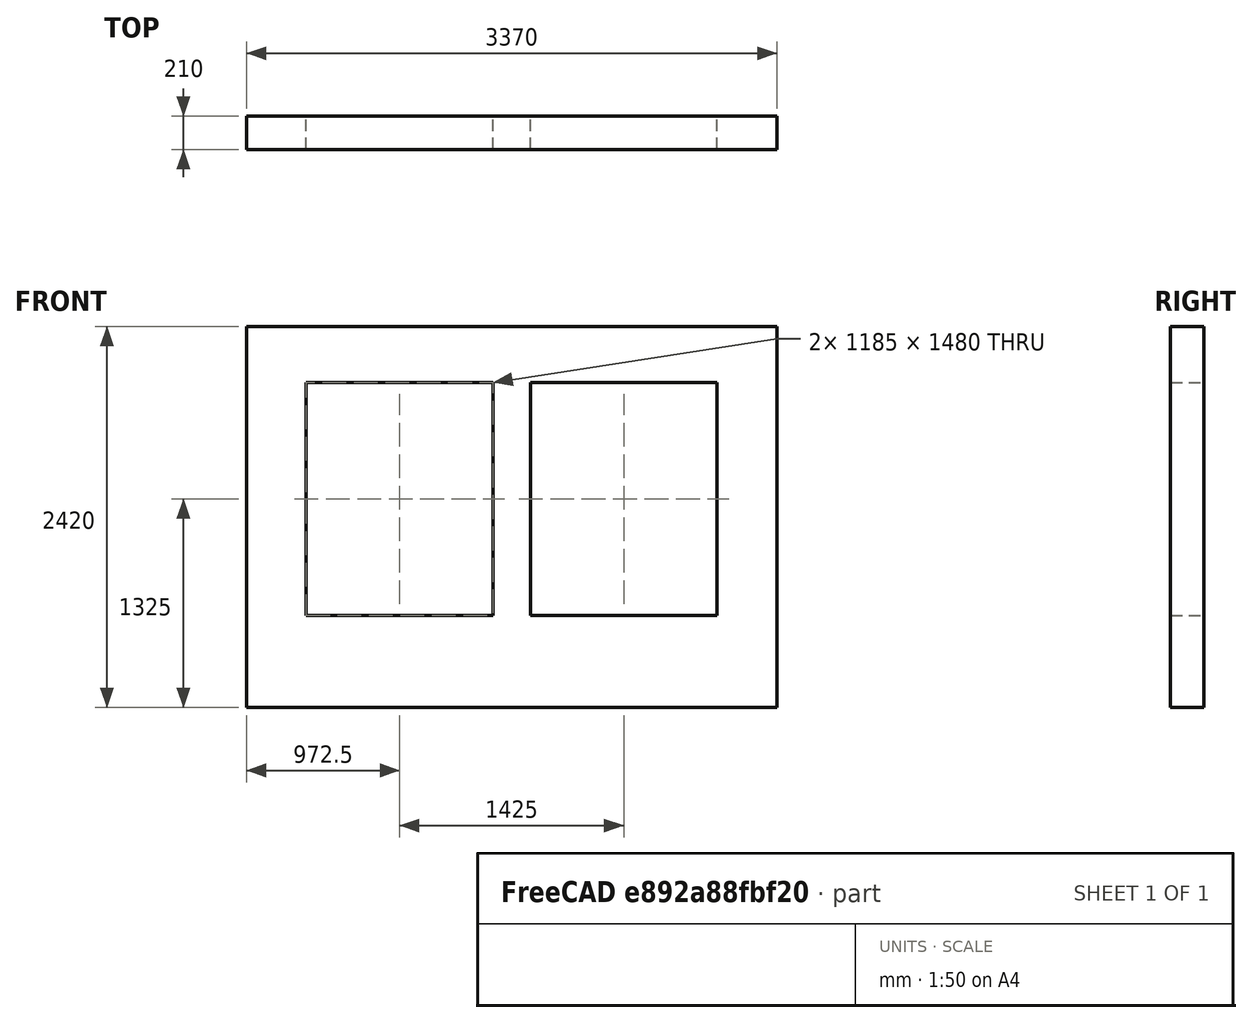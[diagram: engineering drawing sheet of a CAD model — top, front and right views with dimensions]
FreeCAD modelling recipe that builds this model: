
FCSTD DOCUMENT  (FreeCAD 0.19R24276 (Git))
Label: frontWall
License: All rights reserved
LicenseURL: http://en.wikipedia.org/wiki/All_rights_reserved
objects: Sketcher::SketchObject×1, PartDesign::Pad×1, PartDesign::Body×1
note: 4 computed .brp shape members not serialized (recipe doc carries the construction recipe); baked Part::Feature solids carry a one-line shape summary decoded from their .brp

FEATURE [Sketcher::SketchObject] Sketch
  FullyConstrained = true
  MapMode = 5
  Placement = pos=(0,0,0) rot=(1,0,0;1.5708rad)
  Support = -> [XZ_Plane]
  sketch-geometry (12):
    g0: LineSegment StartX=0 StartY=0 StartZ=0 EndX=3370 EndY=0 EndZ=0
    g1: LineSegment StartX=3370 StartY=0 StartZ=0 EndX=3370 EndY=2420 EndZ=0
    g2: LineSegment StartX=3370 StartY=2420 StartZ=0 EndX=0 EndY=2420 EndZ=0
    g3: LineSegment StartX=0 StartY=2420 StartZ=0 EndX=0 EndY=0 EndZ=0
    g4: LineSegment StartX=380 StartY=2065 StartZ=0 EndX=1565 EndY=2065 EndZ=0
    g5: LineSegment StartX=1565 StartY=2065 StartZ=0 EndX=1565 EndY=585 EndZ=0
    g6: LineSegment StartX=1565 StartY=585 StartZ=0 EndX=380 EndY=585 EndZ=0
    g7: LineSegment StartX=380 StartY=585 StartZ=0 EndX=380 EndY=2065 EndZ=0
    g8: LineSegment StartX=1805 StartY=2065 StartZ=0 EndX=2990 EndY=2065 EndZ=0
    g9: LineSegment StartX=2990 StartY=2065 StartZ=0 EndX=2990 EndY=585 EndZ=0
    g10: LineSegment StartX=2990 StartY=585 StartZ=0 EndX=1805 EndY=585 EndZ=0
    g11: LineSegment StartX=1805 StartY=585 StartZ=0 EndX=1805 EndY=2065 EndZ=0
  constraints (35):
    c: Coincident(g0,g1)
    c: Coincident(g1,g2)
    c: Coincident(g2,g3)
    c: Coincident(g3,g0)
    c: Horizontal(g0)
    c: Horizontal(g2)
    c: Vertical(g1)
    c: Vertical(g3)
    c: Coincident(g0,g-1)
    c: DistanceX(g0,g0) = 3370
    c: DistanceY(g3,g3) = 2420
    c: Coincident(g4,g5)
    c: Coincident(g5,g6)
    c: Coincident(g6,g7)
    c: Coincident(g7,g4)
    c: Horizontal(g4)
    c: Horizontal(g6)
    c: Vertical(g5)
    c: Vertical(g7)
    c: Coincident(g8,g9)
    c: Coincident(g9,g10)
    c: Coincident(g10,g11)
    c: Coincident(g11,g8)
    c: Horizontal(g8)
    c: Horizontal(g10)
    c: Vertical(g9)
    c: Vertical(g11)
    c: DistanceY(g0,g6) = 585
    c: Horizontal(g10,g5)
    c: DistanceX(g0,g6) = 380
    c: DistanceY(g6,g4) = 1480
    c: Equal(g7,g11)
    c: DistanceX(g6,g5) = 1185
    c: Equal(g6,g10)
    c: DistanceX(g5,g10) = 240
FEATURE [PartDesign::Pad] Pad
  Direction = (1,1,1)
  Length = 210
  Length2 = 100
  Placement = pos=(0,0,0) rot=(1,0,0;1.5708rad)
  Profile = -> Sketch
  Reversed = true
  Type = 0
FEATURE [PartDesign::Body] Body
  Group = -> [Sketch,Pad]
  Origin = -> Origin
  Tip = -> Pad
